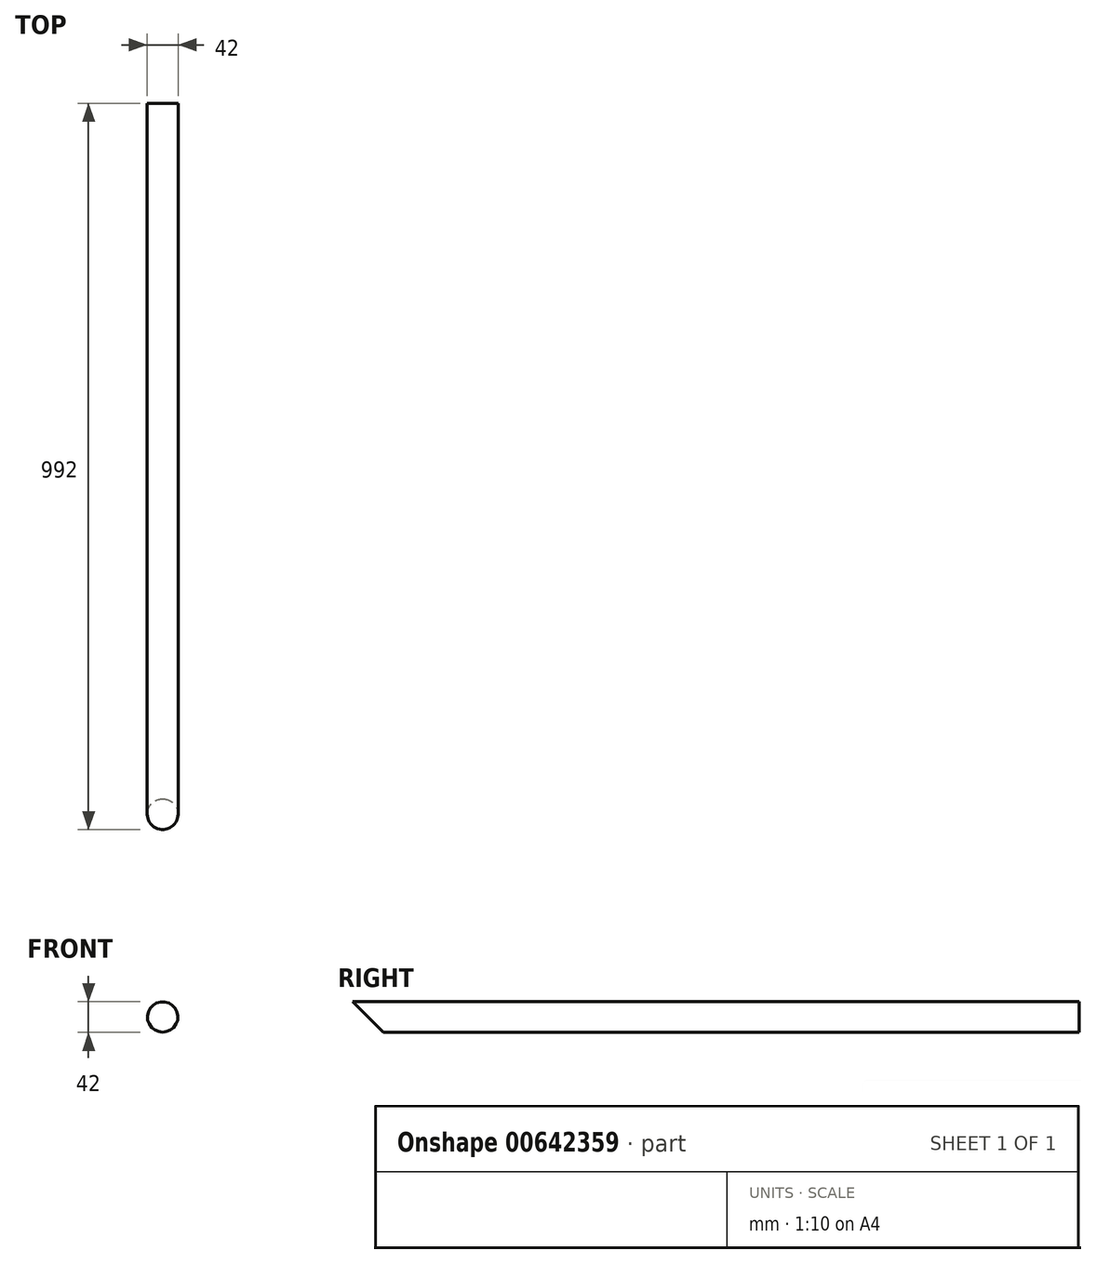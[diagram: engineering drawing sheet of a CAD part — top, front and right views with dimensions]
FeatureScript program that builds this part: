
annotation { "Feature Type Name" : "Feature", "Feature Type Description" : "" }
export const myFeature = defineFeature(function(context is Context, id is Id, definition is map)
    precondition{}
    {
        {
            var Q0;
            Q0=qCreatedBy(makeId("Front.planeOp"),FACE);
            var sketch = newSketch(context, id + "F0", { "sketchPlane" : qUnion([Q0])});
            skLineSegment(sketch, "E0.bottom", {"start": v(21, 21) * mm, "end": v(-21, 21) * mm});
            skLineSegment(sketch, "E0.top", {"start": v(21, -21) * mm, "end": v(-21, -21) * mm});
            skLineSegment(sketch, "E0.left", {"start": v(21, 21) * mm, "end": v(21, -21) * mm});
            skLineSegment(sketch, "E0.right", {"start": v(-21, 21) * mm, "end": v(-21, -21) * mm});
            skPoint(sketch, "E0.middle", {"position": v(0, 0) * mm});
            skSolve(sketch);
        }
        {
            var Q0;
            Q0=makeQuery(id+"F0.imprint","IMPRINT",FACE,{"disambiguationData":[TD([[makeQuery(id+"F0.imprint","IMPRINT",EDGE,{"derivedFrom":sQuery(id+"F0.wireOp",EDGE,"E0.bottom")}),1.0]])]});
            extrude(context, id + "F1", {"entities" : qUnion([Q0]), "depth" : 992 * mm, "offsetDistance" : 25 * mm});
        }
        {
            var Q0;
            Q0=makeQuery(id+"F1.opExtrude","SWEPT_FACE",FACE,{"disambiguationData":[OSD([sQuery(id+"F0.wireOp",EDGE,"E0.left")])]});
            var sketch = newSketch(context, id + "F2", { "sketchPlane" : qUnion([Q0])});
            skLineSegment(sketch, "E1", {"start": v(-992, 21) * mm, "end": v(-950, -21) * mm});
            skSolve(sketch);
        }
        {
            var Q0;
            {var subQ0=sQuery(id+"F2.wireOp",EDGE,"E1");Q0=makeQuery(id+"F2.imprint","IMPRINT",FACE,{"disambiguationData":[TD([[makeQuery(id+"F2.imprint","IMPRINT",EDGE,{"derivedFrom":subQ0}),-1.0]])]});}
            extrude(context, id + "F3", {"entities" : qUnion([Q0]), "operationType" : NewBodyOperationType.REMOVE, "oppositeDirection" : true, "depth" : 100 * mm, "offsetDistance" : 25 * mm});
        }
        {
            var Q0;
            Q0=makeQuery(id+"F1.opExtrude","SWEPT_EDGE",EDGE,{"disambiguationData":[OSD([sQuery(id+"F0.wireOp",EDGE,"E0.bottom"),sQuery(id+"F0.wireOp",EDGE,"E0.right")])]});
            var Q1;
            Q1=makeQuery(id+"F1.opExtrude","SWEPT_EDGE",EDGE,{"disambiguationData":[OSD([sQuery(id+"F0.wireOp",EDGE,"E0.top"),sQuery(id+"F0.wireOp",EDGE,"E0.right")])]});
            var Q2;
            Q2=makeQuery(id+"F1.opExtrude","SWEPT_EDGE",EDGE,{"disambiguationData":[OSD([sQuery(id+"F0.wireOp",EDGE,"E0.bottom"),sQuery(id+"F0.wireOp",EDGE,"E0.left")])]});
            var Q3;
            Q3=makeQuery(id+"F1.opExtrude","SWEPT_EDGE",EDGE,{"disambiguationData":[OSD([sQuery(id+"F0.wireOp",EDGE,"E0.top"),sQuery(id+"F0.wireOp",EDGE,"E0.left")])]});
            fillet(context, id + "F4", {"entities" : qUnion([Q0, Q1, Q2, Q3]), "radius" : 21 * mm, "tangentPropagation" : true, "allowEdgeOverflow" : false});
        }
    });
